# Revit family: Sanitary_Shower-screens_Duscholux_D2Swing_Two-fixed-segments+pivot-twin-doors-shower
name_source: partatom
category: Aparatos sanitarios
units: mm (PartAtom-declared; Revit-internal decimal feet)

## family parameters
Compartido = No
Corte con vacíos al cargar = No
Cota de conector redondo = Diámetro de uso
Número OmniClass = 23.45.00.00
Punto de cálculo de habitación = No
Se basa en plano de trabajo = No
Siempre vertical = Sí
Tipo de pieza = Normal
Título OmniClass = Sanitary, Laundry, and Cleaning Equipment

## types (3) — shared parameters
Certified Quality UNE EN 14428 = http://www.duscholux.es
Combinations = Lateral 90°
Components = Eropean components
Configuration enclosure = http://configuratumampara.duscholux.es
Código de montaje = C1030200
Descripción = 2 fixed segments + pivot twin doors at 180º for shower
Door aperture = 620 mm  [stored 2.03412 ft]
Environmental Management ISO 14001 = ECOEMBES Certificate
Fabricante = Duscholux Ibérica, S.A.
Fact Sheet = https://www.duscholux.es
Glass Material = Glass_Material-Duscholux
Glass in Building UNE EN 12150 = CE Conformity marking
Handle Height = 1000 mm  [stored 3.28084 ft]
Height = 2000 mm  [stored 6.56168 ft]
Image = https://www.duscholux.es
Maintenance and Cleaning = https://www.duscholux.es
Max Height = 2000 mm  [stored 6.56168 ft]
Min Max Width = 1600 mm  [stored 5.24934 ft]
Min Max Width fixed segment = 180 mm  [stored 0.590551 ft]
Modelo = D2 Swing
Opening System = Pivot Doors
Opening System Image = http://blob.duscholux.es
Opening left angle = 0.00°
Opening right angle = 0.00°
Products = http://www.duscholux.es
Ref. = S3C
Series = D2
Technical Inspection Certificate (Applus) = https://www.duscholux.es
Thickness Glass = 5 mm  [stored 0.0164042 ft]
URL = http://www.duscholux.es
Visibility Wall Support = No
Width = 1600 mm  [stored 5.24934 ft]
Width fixed segment = 180 mm  [stored 0.590551 ft]

## per-type parameters (varying)
| type | Accesories Material | Frame Material | Handle Material |
| Matte Silver Aluminium Finish | Plastic_Duscholux Material-Gray Finish | Anodized Aluminium_Duscholux Material-Matte Silver Finish | Zamac_Duscholux Material-Matte Silver Finish |
| Shiny Silver Aluminium Finish | Plastic_Duscholux Material-Gray Finish | Anodized Aluminium_Duscholux Material-Shiny Silver Finish | Zamac_Duscholux Material-Chrome Finish |
| Black Aluminium Finish | Plastic_Duscholux Material-Black Finish | Anodized Aluminium_Duscholux Material-Black Finish | Anodized Aluminium_Duscholux Material-Black Finish |

note: [stored X ft] marks values corroborated as IEEE doubles in the binary element streams (Revit-internal decimal feet)

## geometry (parser evidence)
native form markers: Sweep x3
no freeform markers — native parametric forms only
